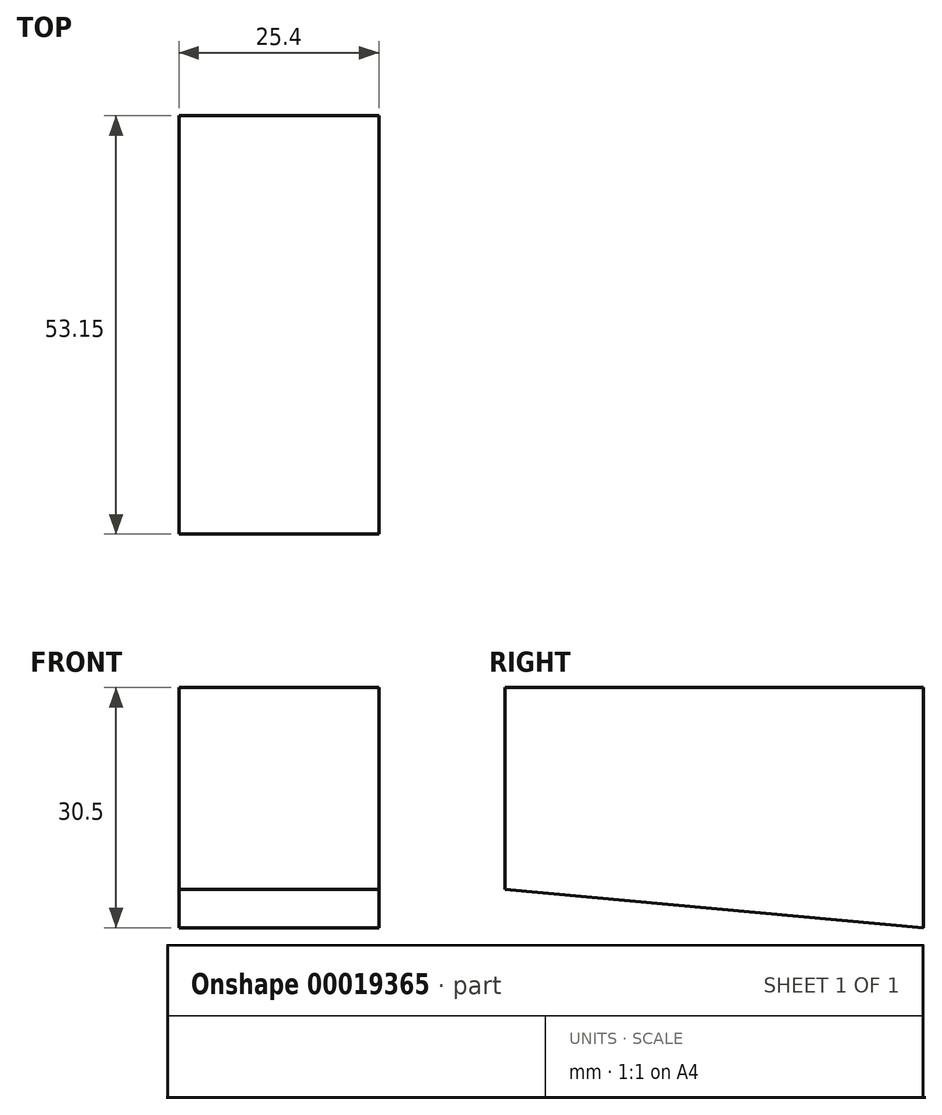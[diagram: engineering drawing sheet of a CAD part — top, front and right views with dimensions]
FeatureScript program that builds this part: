
annotation { "Feature Type Name" : "Feature", "Feature Type Description" : "" }
export const myFeature = defineFeature(function(context is Context, id is Id, definition is map)
    precondition{}
    {
        {
            var Q0;
            Q0=qCreatedBy(makeId("Right.planeOp"),FACE);
            var sketch = newSketch(context, id + "F0", { "sketchPlane" : qUnion([Q0])});
            skLineSegment(sketch, "E0", {"start": v(20.78, 9.98) * mm, "end": v(20.78, 40.48) * mm});
            skLineSegment(sketch, "E1", {"start": v(20.78, 40.48) * mm, "end": v(-32.37, 40.48) * mm});
            skLineSegment(sketch, "E2", {"start": v(-32.37, 40.48) * mm, "end": v(-32.37, 14.87) * mm});
            skLineSegment(sketch, "E3", {"start": v(-32.37, 14.87) * mm, "end": v(20.78, 9.98) * mm});
            skSolve(sketch);
        }
        {
            var Q0;
            Q0 = qSketchRegion(id + "F0", true);
            extrude(context, id + "F1", {"entities" : qUnion([Q0]), "depth" : 25.4 * mm});
        }
    });
